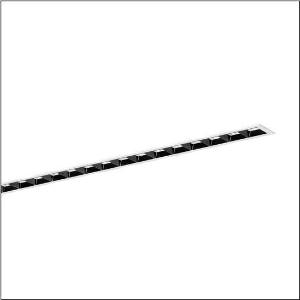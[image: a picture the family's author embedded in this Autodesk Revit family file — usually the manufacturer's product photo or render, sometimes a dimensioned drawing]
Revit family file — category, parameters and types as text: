
# Revit family: silica_r__21_51mx12da34wb_5af2
name_source: partatom
category: Lighting Fixtures
units: mm (PartAtom-declared; Revit-internal decimal feet)

## family parameters
Cut with Voids When Loaded = No
Host = Face
Light Source = No
Part Type = Normal
Room Calculation Point = No
Round Connector Dimension = Use Diameter
Shared = No

## types (1)
- --- (1 x LED, 4320 lm, 27.4 W, 3000K)
    Apparent Load = 27 VA
    CIE Flux Codes = 86 100 100 100 100
    Color Rendering = 80
    Color Temperature = 3000K
    Default Elevation = 1800 mm
    Description = Silica® 21, office luminaire, primary light control with darklight reflector, of PMMA, black, CAT 2 (L<= 3000cd/m²), light emission: direct distribution, primary light characteristic: symmetric, installation type: recessed, LED, rated luminous flux: 4.320lm, luminous efficacy: 158lm/W, light colour: 830, colour temperature: 3000K, with terminal, 3+2-pole, max. 2.5mm², mains connection: 220..240V, AC, 50/60Hz, rated input power: 27.4W, luminaire housing, of aluminium, traffic white (RAL 9016), length: 1.228mm, width: 79mm, height: 53mm, protection rating (complete): IP20, insulation class (complete): insulation class I (protective earthing), certification: CE, permissible operating ambient temperature: 0..+35°C, standard: EN 50419, packaging unit: 1 piece
    Height = 0 mm  [stored 0 ft]
    Lamp = 1 x LED
    Lamp Light Flux = 4320 lm
    Lamp Power = 27.4 W
    Lamp count = 1
    Length = 1227 mm
    Luminous efficacy = 158 lm/W
    Manufacturer = Siteco
    ModVariant = No
    Model = 51MX12DA34WB
    Mounting Place = Ceiling
    Mounting Type = Recessed
    Number of Poles = 1
    OnlyDefault = Yes
    Power Factor = 1
    Product Name = Silica® 21
    Product group = office luminaire | ceiling recessed
    ProductGroupID = 401
    Protection Class = Protection class I
    Protection Degree = IP 20
    RLX_Detail_Level = 1
    RLX_Emergency_Light_Flux = 0 lm
    RLX_Emergency_Type = 0
    RLX_Emergency_Type_DB = No
    RlxData = <blob elided: 39517 chars, md5=855a7dd2>
    Socket = socket
    Standby Power = 0 W
    System Light Flux = 4320 lm
    System Power = 27 W
    Type Comments = factory setting: luminous flux: 100 % | dim-lin: 254 | 392 mA
    Type Image = l_1297791.jpg
    URL = http://relux.com
    VarID = @adj_055703
    Voltage = 0 V
    Weight = 0.00 kg
    Width = 79 mm

note: [stored X ft] marks values corroborated as IEEE doubles in the binary element streams (Revit-internal decimal feet)

## geometry (parser evidence)
native form markers: Blend x4, Sweep x11
no freeform markers — native parametric forms only
